# Revit family: Network Video Endpoint-Q-SYS-NV-21-HU
name_source: partatom
category: Communication Devices
units: mm (PartAtom-declared; Revit-internal decimal feet)

## family parameters
Cut with Voids When Loaded = No
Host = Face
Maintain Annotation Orientation = No
OmniClass Number = 23.85.10.14
OmniClass Title = Visual Information Systems
Part Type = Normal
Room Calculation Point = No
Round Connector Dimension = Use Diameter
Shared = No

## types (2) — shared parameters
Apparent Load = 120 VA
Body Height = 30.5 mm  [stored 0.100066 ft]
Body Material = Paint - Q-SYS - Black
Body Width = 187.4 mm  [stored 0.614829 ft]
Default Elevation = 1219.2 mm  [stored 4 ft]
Depth = 131.5 mm  [stored 0.43143 ft]
Description = Native Network Video Endpoint for Q-SYS.
Frame Depth = 2 mm  [stored 0.00656168 ft]
Frame Height = 30.5 mm  [stored 0.100066 ft]
Grille Material = Paint - Q-SYS - Black Mesh
Height = 30.5 mm  [stored 0.100066 ft]
Highlight Material = Plastic - Q-SYS - Black
IQ Category = Video Endpoint
Intake Y Offset = 17 mm
LED Material = Plastic - Q-SYS - LED Blue
Load Classification = Other
Manufacturer = Q-SYS
Manufacturer URL = https://www.qsys.com
Minimum Circuit Amps = 9 A
Model = NV-21-HU
Number of Poles = 2
Power Factor = 0.9
Product Documentation Link = https://www.qsys.com
Product Page URL = https://www.qsys.com
URL = https://www.qsys.com
Voltage = 12 V
Weight = 1.75 lbm
Weight Dimensional = 1.75
Weight Product = 1.75
Width = 215 mm
zero-valued in all types: Current Draw

## per-type parameters (varying)
| type | Body Offset | Button X Offset | Button Y Offset | Intake X Offset | LED 1 Y Offset | LED 2 Y Offset | LED X Offset |
| On Surface | 0 mm  [stored 0 ft] | 157.4 mm  [stored 0.516404 ft] | 10.5 mm  [stored 0.0344488 ft] | 23 mm  [stored 0.0754593 ft] | 20.5 mm  [stored 0.0672572 ft] | 15.5 mm  [stored 0.050853 ft] | 172.4 mm  [stored 0.565617 ft] |
| Under Surface | 12 mm  [stored 0.0393701 ft] | 30 mm  [stored 0.0984252 ft] | 20 mm  [stored 0.0656168 ft] | 104.4 mm  [stored 0.34252 ft] | 10 mm  [stored 0.0328084 ft] | 15 mm  [stored 0.0492126 ft] | 15 mm  [stored 0.0492126 ft] |

note: column(s) folded — value = type name in every type: Type Comments

type visibility flags: 2 boolean params named "<type name>" — each type sets only its own to Yes (folded from table)

note: [stored X ft] marks values corroborated as IEEE doubles in the binary element streams (Revit-internal decimal feet)

## geometry (parser evidence)
native form markers: Sweep x1
no freeform markers — native parametric forms only
